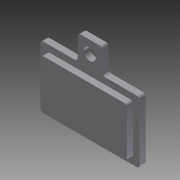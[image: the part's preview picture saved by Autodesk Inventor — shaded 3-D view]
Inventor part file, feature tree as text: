
AUTODESK INVENTOR PART (.ipt)
format: ipt  version: 2011 (Build 150239000, 239)  size: 120,320 bytes
history: native  units: in
note: dims shown in document units (in); Inventor stores cm internally (conversion verified against a paired STEP export)
features: sketch x4, extrude x3, hole x1, fillet x1
ambient origin geometry x8: Origin, YZ Plane, XZ Plane, XY Plane, X Axis, Y Axis, Z Axis, Center Point
bodies: Solid1 (feature_tree)
feature tree (9):
  extrude  "Extrusion1"  Depth=0.3937in
  extrude  "Extrusion2"  Depth=0.0413in
  extrude  "Extrusion3"  Depth=0.1575in
  hole  "Hole1"  [1 undecoded]
  fillet  "Fillet1"  Radius=0.0197in
  sketch  "Sketch1"  dims[d0=0.6299in d1=0.3937in]
  sketch  "Sketch2"  dims[d2=0.0787in d3=0.0in d4=0.0413in]
  sketch  "Sketch3"  dims[d5=0.0394in d6=0.0in d7=0.1575in]
  sketch  "Sketch4"  dims[d8=0.2362in d9=0.1575in d10=0.0in d11=0.075in d12=0.75in d13=0.375in d14=0.25in d15=0.5635in d16=1.0in d17=0.8108in d18=0.0197in]
note: 1 required parameter value undecoded (feature->parameter linkage not recoverable at this tier; creation-order binding heuristic only, values carry confidence <= 0.55)
